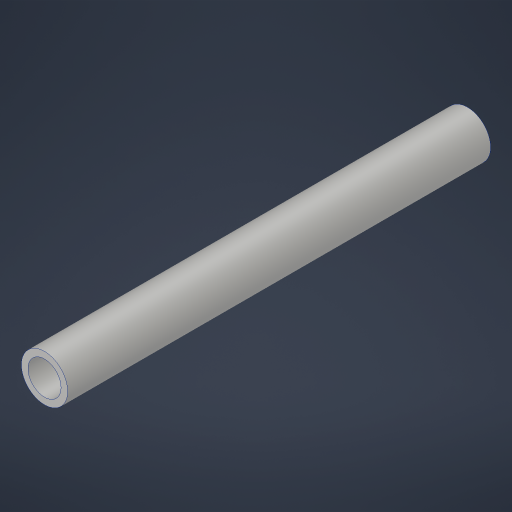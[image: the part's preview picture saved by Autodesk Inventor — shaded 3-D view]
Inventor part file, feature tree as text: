
AUTODESK INVENTOR PART (.ipt)
format: ipt  version: 2023.4 (Build 274418000, 418)  size: 171,008 bytes
history: native  units: in
note: dims shown in document units (in); Inventor stores cm internally (conversion verified against a paired STEP export)
features: extrude x1, sketch x1
ambient origin geometry x8: Origin, YZ Plane, XZ Plane, XY Plane, X Axis, Y Axis, Z Axis, Center Point
bodies: Solid1 (feature_tree)
feature tree (2):
  extrude  "Extrusion1"  Depth=8.0in
  sketch  "Sketch1"  dims[d0=0.875in d1=0.125in d2=8.0in d3=0.0in]
